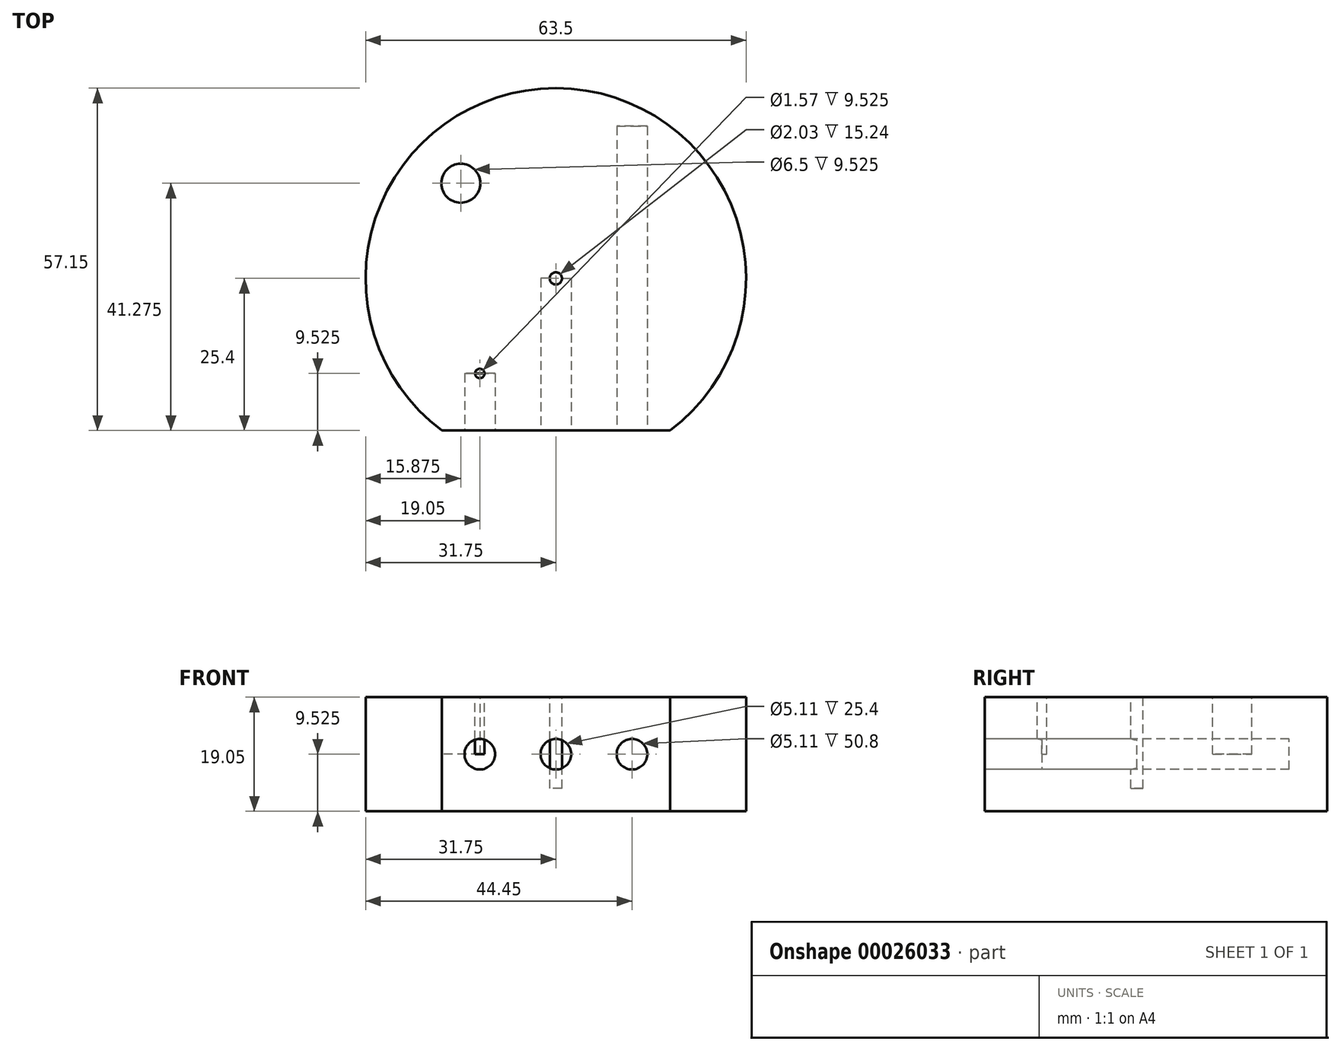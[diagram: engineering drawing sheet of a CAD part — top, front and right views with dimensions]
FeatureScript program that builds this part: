
annotation { "Feature Type Name" : "Feature", "Feature Type Description" : "" }
export const myFeature = defineFeature(function(context is Context, id is Id, definition is map)
    precondition{}
    {
        {
            var Q0;
            Q0=qCreatedBy(makeId("Top.planeOp"),FACE);
            var sketch = newSketch(context, id + "F0", { "sketchPlane" : qUnion([Q0])});
            skCircle(sketch, "E0", {"center": v(0, 0) * mm, "radius": 31.75 * mm});
            skSolve(sketch);
        }
        {
            var Q0;
            Q0 = qSketchRegion(id + "F0", true);
            extrude(context, id + "F1", {"entities" : qUnion([Q0]), "depth" : 19.05 * mm});
        }
        {
            var Q0;
            Q0=makeQuery(id+"F1.opExtrude","CAP_FACE",FACE,{"disambiguationData":[OSD([sQuery(id+"F0.wireOp",EDGE,"E0")])],"isStart":false});
            var sketch = newSketch(context, id + "F2", { "sketchPlane" : qUnion([Q0])});
            skLineSegment(sketch, "E1", {"start": v(-19.05, -25.4) * mm, "end": v(19.05, -25.4) * mm});
            skSolve(sketch);
        }
        {
            var Q0;
            {var subQ1=sQuery(id+"F2.wireOp",EDGE,"E1");Q0=makeQuery(id+"F2.imprint","IMPRINT",FACE,{"disambiguationData":[TD([[makeQuery(id+"F2.imprint","IMPRINT",EDGE,{"derivedFrom":subQ1}),-1.0]])]});}
            extrude(context, id + "F3", {"entities" : qUnion([Q0]), "operationType" : NewBodyOperationType.REMOVE, "oppositeDirection" : true, "depth" : 25.4 * mm});
        }
        {
            var Q0;
            Q0=makeQuery(id+"F3.boolean.opBoolean","COPY",FACE,{"derivedFrom":makeQuery(id+"F3.opExtrude","SWEPT_FACE",FACE,{"disambiguationData":[OSD([sQuery(id+"F2.wireOp",EDGE,"E1")])]})});
            var sketch = newSketch(context, id + "F4", { "sketchPlane" : qUnion([Q0])});
            skCircle(sketch, "E2", {"center": v(0, 9.52) * mm, "radius": 2.55 * mm});
            skLineSegment(sketch, "E3", {"start": v(-19.05, 9.52) * mm, "end": v(19.05, 9.52) * mm, "construction": true});
            skSolve(sketch);
        }
        {
            var Q0;
            Q0=makeQuery(id+"F4.imprint","IMPRINT",FACE,{"disambiguationData":[TD([[makeQuery(id+"F4.imprint","IMPRINT",EDGE,{"derivedFrom":sQuery(id+"F4.wireOp",EDGE,"E2")}),1.0]])]});
            extrude(context, id + "F5", {"entities" : qUnion([Q0]), "operationType" : NewBodyOperationType.REMOVE, "oppositeDirection" : true, "depth" : 25.4 * mm});
        }
        {
            var Q0;
            Q0=makeQuery(id+"F3.boolean.opBoolean","COPY",FACE,{"derivedFrom":makeQuery(id+"F3.opExtrude","SWEPT_FACE",FACE,{"disambiguationData":[OSD([sQuery(id+"F2.wireOp",EDGE,"E1")])]})});
            var sketch = newSketch(context, id + "F6", { "sketchPlane" : qUnion([Q0])});
            skCircle(sketch, "E4", {"center": v(-12.7, 9.52) * mm, "radius": 2.55 * mm});
            skLineSegment(sketch, "E5", {"start": v(-19.05, 9.52) * mm, "end": v(19.05, 9.52) * mm, "construction": true});
            skLineSegment(sketch, "E6", {"start": v(0, 19.05) * mm, "end": v(0, 0) * mm, "construction": true});
            skSolve(sketch);
        }
        {
            var Q0;
            Q0=makeQuery(id+"F6.imprint","IMPRINT",FACE,{"disambiguationData":[TD([[makeQuery(id+"F6.imprint","IMPRINT",EDGE,{"derivedFrom":sQuery(id+"F6.wireOp",EDGE,"E4")}),1.0]])]});
            extrude(context, id + "F7", {"entities" : qUnion([Q0]), "operationType" : NewBodyOperationType.REMOVE, "oppositeDirection" : true, "depth" : 9.52 * mm});
        }
        {
            var Q0;
            Q0=makeQuery(id+"F1.opExtrude","CAP_FACE",FACE,{"disambiguationData":[OSD([sQuery(id+"F0.wireOp",EDGE,"E0")])],"isStart":false});
            var sketch = newSketch(context, id + "F8", { "sketchPlane" : qUnion([Q0])});
            skCircle(sketch, "E7", {"center": v(-12.7, -15.88) * mm, "radius": 0.79 * mm});
            skLineSegment(sketch, "E8", {"start": v(0, -25.4) * mm, "end": v(0, 16.24) * mm, "construction": true});
            skSolve(sketch);
        }
        {
            var Q0;
            Q0 = qSketchRegion(id + "F8", true);
            extrude(context, id + "F9", {"entities" : qUnion([Q0]), "operationType" : NewBodyOperationType.REMOVE, "oppositeDirection" : true, "depth" : 9.52 * mm});
        }
        {
            var Q0;
            Q0=makeQuery(id+"F1.opExtrude","CAP_FACE",FACE,{"disambiguationData":[OSD([sQuery(id+"F0.wireOp",EDGE,"E0")])],"isStart":false});
            var sketch = newSketch(context, id + "F10", { "sketchPlane" : qUnion([Q0])});
            skCircle(sketch, "E9", {"center": v(0, 0) * mm, "radius": 1.02 * mm});
            skSolve(sketch);
        }
        {
            var Q0;
            Q0 = qSketchRegion(id + "F10", true);
            extrude(context, id + "F11", {"entities" : qUnion([Q0]), "operationType" : NewBodyOperationType.REMOVE, "oppositeDirection" : true, "depth" : 15.24 * mm});
        }
        {
            var Q0;
            Q0=makeQuery(id+"F3.boolean.opBoolean","COPY",FACE,{"derivedFrom":makeQuery(id+"F3.opExtrude","SWEPT_FACE",FACE,{"disambiguationData":[OSD([sQuery(id+"F2.wireOp",EDGE,"E1")])]})});
            var sketch = newSketch(context, id + "F12", { "sketchPlane" : qUnion([Q0])});
            skLineSegment(sketch, "E10", {"start": v(-19.05, 9.52) * mm, "end": v(19.05, 9.52) * mm, "construction": true});
            skLineSegment(sketch, "E11", {"start": v(19.05, 9.52) * mm, "end": v(0, 19.05) * mm, "construction": true});
            skLineSegment(sketch, "E12", {"start": v(0, 19.05) * mm, "end": v(0, 0) * mm, "construction": true});
            skCircle(sketch, "E13", {"center": v(12.7, 9.52) * mm, "radius": 2.55 * mm});
            skSolve(sketch);
        }
        {
            var Q0;
            Q0 = qSketchRegion(id + "F12", true);
            extrude(context, id + "F13", {"entities" : qUnion([Q0]), "operationType" : NewBodyOperationType.REMOVE, "oppositeDirection" : true, "depth" : 50.8 * mm});
        }
        {
            var Q0;
            Q0=makeQuery(id+"F1.opExtrude","CAP_FACE",FACE,{"disambiguationData":[OSD([sQuery(id+"F0.wireOp",EDGE,"E0")])],"isStart":false});
            var sketch = newSketch(context, id + "F14", { "sketchPlane" : qUnion([Q0])});
            skCircle(sketch, "E14", {"center": v(-15.88, 15.88) * mm, "radius": 3.25 * mm});
            skLineSegment(sketch, "E15", {"start": v(0, 31.75) * mm, "end": v(0, -31.69) * mm, "construction": true});
            skLineSegment(sketch, "E16", {"start": v(0, -31.69) * mm, "end": v(-45.14, 0) * mm, "construction": true});
            skLineSegment(sketch, "E17", {"start": v(-45.14, 0) * mm, "end": v(46.02, 0) * mm, "construction": true});
            skSolve(sketch);
        }
        {
            var Q0;
            Q0=makeQuery(id+"F14.imprint","IMPRINT",FACE,{"disambiguationData":[TD([[makeQuery(id+"F14.imprint","IMPRINT",EDGE,{"derivedFrom":sQuery(id+"F14.wireOp",EDGE,"E14")}),1.0]])]});
            extrude(context, id + "F15", {"entities" : qUnion([Q0]), "operationType" : NewBodyOperationType.REMOVE, "oppositeDirection" : true, "depth" : 9.52 * mm});
        }
    });
